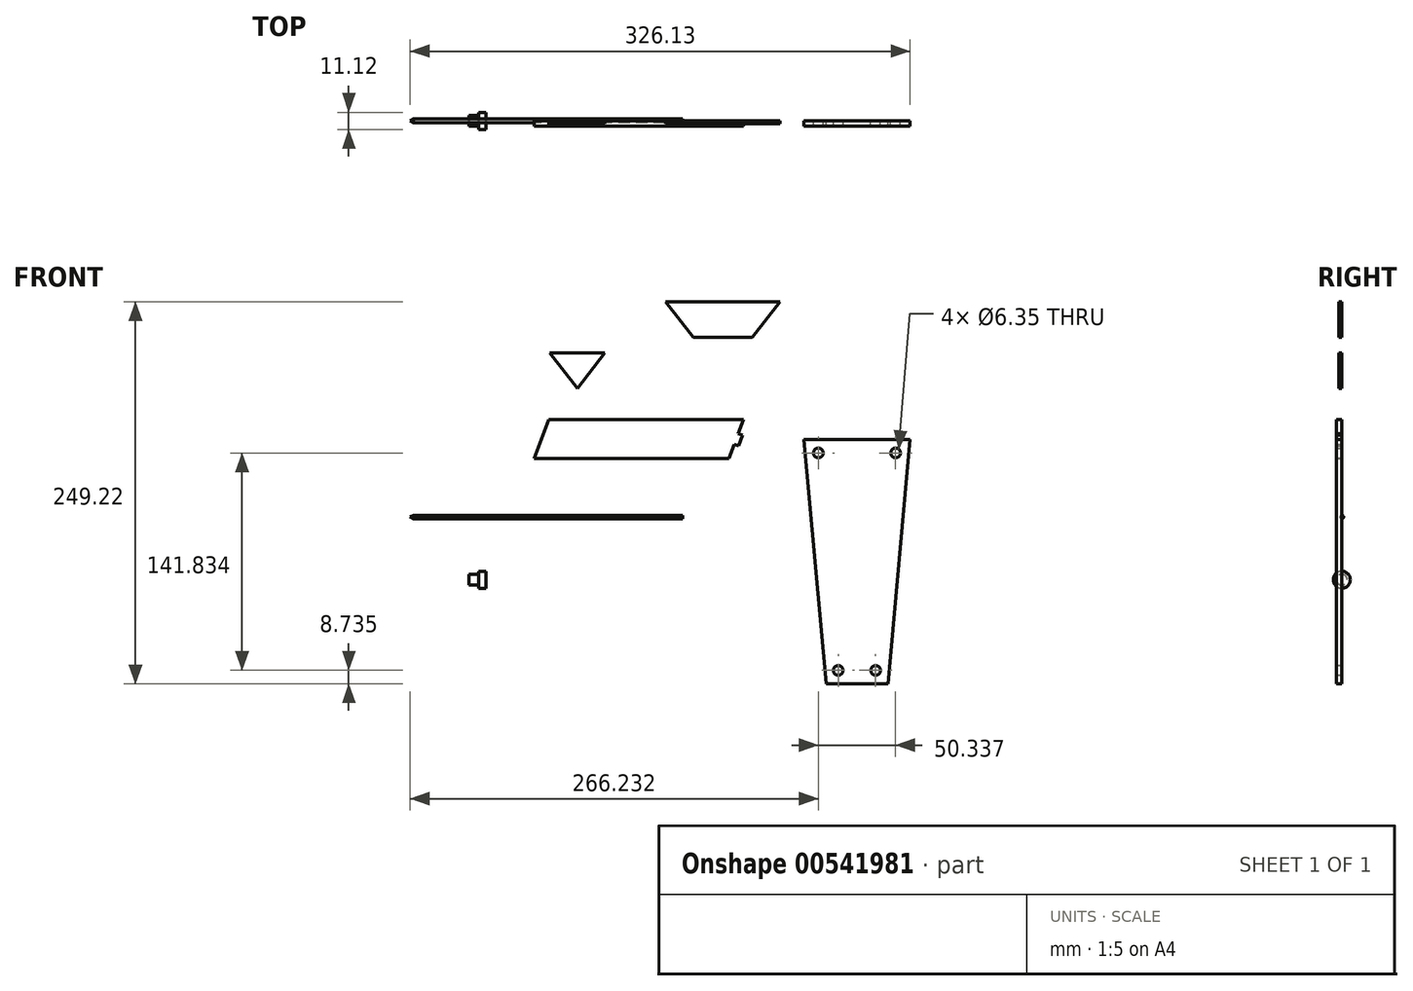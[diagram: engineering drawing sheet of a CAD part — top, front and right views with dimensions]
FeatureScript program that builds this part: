
annotation { "Feature Type Name" : "Feature", "Feature Type Description" : "" }
export const myFeature = defineFeature(function(context is Context, id is Id, definition is map)
    precondition{}
    {
        {
            var Q0;
            Q0=qCreatedBy(makeId("Front.planeOp"),FACE);
            var sketch = newSketch(context, id + "F0", { "sketchPlane" : qUnion([Q0])});
            skLineSegment(sketch, "E0.bottom", {"start": v(11.82, -12.27) * mm, "end": v(-115.18, -12.27) * mm});
            skLineSegment(sketch, "E0.top", {"start": v(21.07, 13.13) * mm, "end": v(-105.93, 13.13) * mm});
            skLineSegment(sketch, "E1", {"start": v(-115.18, -12.27) * mm, "end": v(-105.93, 13.13) * mm});
            skLineSegment(sketch, "E2", {"start": v(21.07, 13.13) * mm, "end": v(17.72, 3.94) * mm});
            skLineSegment(sketch, "E3", {"start": v(15.17, -3.08) * mm, "end": v(18.15, -4.16) * mm});
            skLineSegment(sketch, "E4", {"start": v(18.15, -4.16) * mm, "end": v(19.43, -0.65) * mm});
            skLineSegment(sketch, "E5", {"start": v(16.44, 0.43) * mm, "end": v(19.43, -0.65) * mm, "construction": true});
            skLineSegment(sketch, "E6.trimOffspring", {"start": v(15.17, -3.08) * mm, "end": v(11.82, -12.27) * mm});
            skLineSegment(sketch, "E7.MirrorCS", {"start": v(20.7, 2.86) * mm, "end": v(19.43, -0.65) * mm});
            skLineSegment(sketch, "E8.MirrorCS", {"start": v(17.72, 3.94) * mm, "end": v(20.7, 2.86) * mm});
            skSolve(sketch);
        }
        {
            var Q0;
            Q0 = qSketchRegion(id + "F0", true);
            extrude(context, id + "F1", {"entities" : qUnion([Q0]), "depth" : 3.42 * mm, "offsetDistance" : 25.4 * mm});
        }
        {
            var Q0;
            Q0=qCreatedBy(makeId("Front.planeOp"),FACE);
            var sketch = newSketch(context, id + "F2", { "sketchPlane" : qUnion([Q0])});
            skLineSegment(sketch, "E9", {"start": v(-105.12, 56.63) * mm, "end": v(-87.16, 33.44) * mm});
            skLineSegment(sketch, "E10", {"start": v(-87.16, 33.44) * mm, "end": v(-87.16, 56.63) * mm, "construction": true});
            skLineSegment(sketch, "E11", {"start": v(-87.16, 56.63) * mm, "end": v(-105.12, 56.63) * mm});
            skLineSegment(sketch, "E12.MirrorCS", {"start": v(-87.16, 56.63) * mm, "end": v(-69.2, 56.63) * mm});
            skLineSegment(sketch, "E13.MirrorCS", {"start": v(-69.2, 56.63) * mm, "end": v(-87.16, 33.44) * mm});
            skSolve(sketch);
        }
        {
            var Q0;
            Q0=makeQuery(id+"F2.imprint","IMPRINT",FACE,{"disambiguationData":[TD([[makeQuery(id+"F2.imprint","IMPRINT",EDGE,{"derivedFrom":sQuery(id+"F2.wireOp",EDGE,"E9")}),1.0]])]});
            extrude(context, id + "F3", {"entities" : qUnion([Q0]), "depth" : 1.9 * mm, "offsetDistance" : 25.4 * mm});
        }
        {
            var Q0;
            Q0=qCreatedBy(makeId("Front.planeOp"),FACE);
            var sketch = newSketch(context, id + "F4", { "sketchPlane" : qUnion([Q0])});
            skLineSegment(sketch, "E14", {"start": v(-29.58, 89.92) * mm, "end": v(-11.62, 66.74) * mm});
            skLineSegment(sketch, "E15", {"start": v(-11.62, 66.74) * mm, "end": v(-11.62, 89.92) * mm, "construction": true});
            skLineSegment(sketch, "E16", {"start": v(-11.62, 89.92) * mm, "end": v(-29.58, 89.92) * mm});
            skLineSegment(sketch, "E17.MirrorCS", {"start": v(-11.62, 89.92) * mm, "end": v(6.34, 89.92) * mm});
            skLineSegment(sketch, "E18.MirrorCS", {"start": v(6.34, 89.92) * mm, "end": v(-11.62, 66.74) * mm});
            skLineSegment(sketch, "E19", {"start": v(7.68, 89.92) * mm, "end": v(7.68, 63.94) * mm, "construction": true});
            skLineSegment(sketch, "E20.MirrorCS", {"start": v(26.98, 89.92) * mm, "end": v(9.02, 89.92) * mm});
            skLineSegment(sketch, "E21.MirrorCS", {"start": v(9.02, 89.92) * mm, "end": v(26.98, 66.74) * mm});
            skLineSegment(sketch, "E22.MirrorCS", {"start": v(26.98, 89.92) * mm, "end": v(44.94, 89.92) * mm});
            skLineSegment(sketch, "E23.MirrorCS", {"start": v(44.94, 89.92) * mm, "end": v(26.98, 66.74) * mm});
            skLineSegment(sketch, "E24", {"start": v(-11.62, 66.74) * mm, "end": v(26.98, 66.74) * mm});
            skLineSegment(sketch, "E25", {"start": v(6.34, 89.92) * mm, "end": v(9.02, 89.92) * mm});
            skSolve(sketch);
        }
        {
            var Q0;
            Q0=makeQuery(id+"F4.imprint","IMPRINT",FACE,{"disambiguationData":[TD([[makeQuery(id+"F4.imprint","IMPRINT",EDGE,{"derivedFrom":sQuery(id+"F4.wireOp",EDGE,"E14")}),1.0]])]});
            var Q1;
            Q1=makeQuery(id+"F4.imprint","IMPRINT",FACE,{"disambiguationData":[TD([[makeQuery(id+"F4.imprint","IMPRINT",EDGE,{"derivedFrom":sQuery(id+"F4.wireOp",EDGE,"E18.MirrorCS")}),1.0]])]});
            var Q2;
            Q2=makeQuery(id+"F4.imprint","IMPRINT",FACE,{"disambiguationData":[TD([[makeQuery(id+"F4.imprint","IMPRINT",EDGE,{"derivedFrom":sQuery(id+"F4.wireOp",EDGE,"E20.MirrorCS")}),1.0]])]});
            extrude(context, id + "F5", {"entities" : qUnion([Q0, Q1, Q2]), "depth" : 1.9 * mm, "offsetDistance" : 25.4 * mm});
        }
        {
            var Q0;
            Q0=qCreatedBy(makeId("Front.planeOp"),FACE);
            var sketch = newSketch(context, id + "F6", { "sketchPlane" : qUnion([Q0])});
            skLineSegment(sketch, "E26", {"start": v(95.21, 0) * mm, "end": v(95.21, -159.3) * mm, "construction": true});
            skLineSegment(sketch, "E27", {"start": v(95.21, -159.3) * mm, "end": v(115.38, -159.3) * mm});
            skLineSegment(sketch, "E28", {"start": v(115.38, -159.3) * mm, "end": v(129.94, 0) * mm});
            skLineSegment(sketch, "E29", {"start": v(129.94, 0) * mm, "end": v(95.21, 0) * mm});
            skLineSegment(sketch, "E30.MirrorCS", {"start": v(60.48, 0) * mm, "end": v(95.21, 0) * mm});
            skLineSegment(sketch, "E31.MirrorCS", {"start": v(75.04, -159.3) * mm, "end": v(60.48, 0) * mm});
            skLineSegment(sketch, "E32.MirrorCS", {"start": v(95.21, -159.3) * mm, "end": v(75.04, -159.3) * mm});
            skCircle(sketch, "E33", {"center": v(70.04, -8.73) * mm, "radius": 5.56 * mm, "construction": true});
            skCircle(sketch, "E34", {"center": v(83.01, -150.56) * mm, "radius": 5.56 * mm, "construction": true});
            skCircle(sketch, "E35", {"center": v(83.01, -150.56) * mm, "radius": 3.18 * mm});
            skCircle(sketch, "E36", {"center": v(70.04, -8.73) * mm, "radius": 3.18 * mm});
            skCircle(sketch, "E37.MirrorC", {"center": v(120.38, -8.73) * mm, "radius": 3.18 * mm});
            skCircle(sketch, "E38.MirrorC", {"center": v(120.38, -8.73) * mm, "radius": 5.56 * mm, "construction": true});
            skCircle(sketch, "E39.MirrorC", {"center": v(107.4, -150.56) * mm, "radius": 5.56 * mm, "construction": true});
            skCircle(sketch, "E40.MirrorC", {"center": v(107.4, -150.56) * mm, "radius": 3.18 * mm});
            skSolve(sketch);
        }
        {
            var Q0;
            Q0=makeQuery(id+"F6.imprint","IMPRINT",FACE,{"disambiguationData":[TD([[makeQuery(id+"F6.imprint","IMPRINT",EDGE,{"derivedFrom":sQuery(id+"F6.wireOp",EDGE,"E27")}),1.0]])]});
            extrude(context, id + "F7", {"entities" : qUnion([Q0]), "depth" : 3.42 * mm, "offsetDistance" : 25.4 * mm});
        }
        {
            var Q0;
            Q0=qCreatedBy(makeId("Front.planeOp"),FACE);
            var sketch = newSketch(context, id + "F8", { "sketchPlane" : qUnion([Q0])});
            skLineSegment(sketch, "E41", {"start": v(-157.88, -87.86) * mm, "end": v(-151.53, -87.86) * mm});
            skLineSegment(sketch, "E42", {"start": v(-151.53, -87.86) * mm, "end": v(-151.53, -85.87) * mm});
            skLineSegment(sketch, "E43", {"start": v(-151.53, -85.87) * mm, "end": v(-146.76, -85.87) * mm});
            skLineSegment(sketch, "E44", {"start": v(-146.76, -85.87) * mm, "end": v(-146.76, -91.43) * mm});
            skLineSegment(sketch, "E45", {"start": v(-146.76, -91.43) * mm, "end": v(-157.88, -91.43) * mm});
            skLineSegment(sketch, "E46", {"start": v(-157.88, -91.43) * mm, "end": v(-157.88, -87.86) * mm});
            skLineSegment(sketch, "E47.MirrorCS", {"start": v(-157.88, -95) * mm, "end": v(-151.53, -95) * mm, "construction": true});
            skLineSegment(sketch, "E48.MirrorCS", {"start": v(-157.88, -91.43) * mm, "end": v(-157.88, -95) * mm, "construction": true});
            skLineSegment(sketch, "E49.MirrorCS", {"start": v(-151.53, -95) * mm, "end": v(-151.53, -96.98) * mm, "construction": true});
            skLineSegment(sketch, "E50.MirrorCS", {"start": v(-151.53, -96.98) * mm, "end": v(-146.76, -96.98) * mm, "construction": true});
            skLineSegment(sketch, "E51.MirrorCS", {"start": v(-146.76, -96.98) * mm, "end": v(-146.76, -91.43) * mm, "construction": true});
            skSolve(sketch);
        }
        {
            var Q0;
            Q0=makeQuery(id+"F8.imprint","IMPRINT",FACE,{"disambiguationData":[TD([[makeQuery(id+"F8.imprint","IMPRINT",EDGE,{"derivedFrom":sQuery(id+"F8.wireOp",EDGE,"E41")}),-1.0]])]});
            var Q1;
            Q1=sQuery(id+"F8.wireOp",EDGE,"E45");
            revolve(context, id + "F9", {"entities" : qUnion([Q0]), "axis" : qUnion([Q1]), "revolveType" : RevolveType.FULL, "oppositeDirection" : true});
        }
        {
            var Q0;
            Q0=qCreatedBy(makeId("Front.planeOp"),FACE);
            var sketch = newSketch(context, id + "F10", { "sketchPlane" : qUnion([Q0])});
            skLineSegment(sketch, "E52", {"start": v(-196.2, -50.51) * mm, "end": v(-18.4, -50.51) * mm});
            skLineSegment(sketch, "E53", {"start": v(-18.4, -50.51) * mm, "end": v(-18.4, -49.32) * mm});
            skLineSegment(sketch, "E54", {"start": v(-18.4, -49.32) * mm, "end": v(-194.13, -49.32) * mm});
            skLineSegment(sketch, "E55", {"start": v(-194.13, -49.32) * mm, "end": v(-196.2, -50.51) * mm});
            skSolve(sketch);
        }
        {
            var Q0;
            Q0=makeQuery(id+"F10.imprint","IMPRINT",FACE,{"disambiguationData":[TD([[makeQuery(id+"F10.imprint","IMPRINT",EDGE,{"derivedFrom":sQuery(id+"F10.wireOp",EDGE,"E52")}),1.0]])]});
            var Q1;
            Q1=sQuery(id+"F10.wireOp",EDGE,"E52");
            revolve(context, id + "F11", {"entities" : qUnion([Q0]), "axis" : qUnion([Q1]), "revolveType" : RevolveType.FULL});
        }
    });
